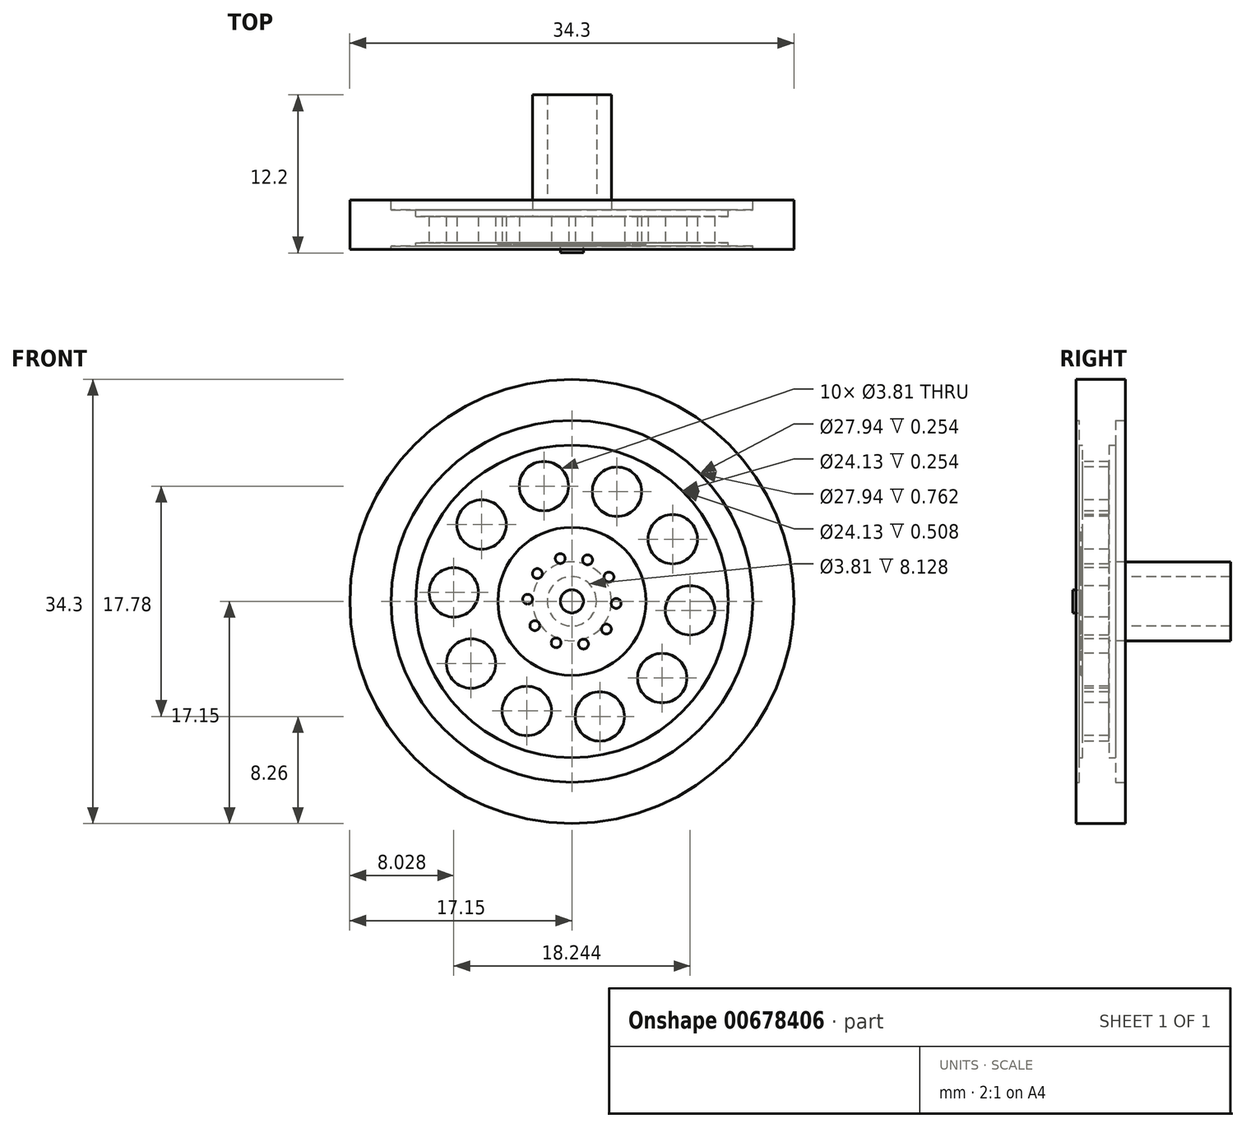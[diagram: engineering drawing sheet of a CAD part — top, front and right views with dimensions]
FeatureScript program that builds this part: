
annotation { "Feature Type Name" : "Feature", "Feature Type Description" : "" }
export const myFeature = defineFeature(function(context is Context, id is Id, definition is map)
    precondition{}
    {
        {
            var Q0;
            Q0=qCreatedBy(makeId("Front.planeOp"),FACE);
            var sketch = newSketch(context, id + "F0", { "sketchPlane" : qUnion([Q0])});
            skCircle(sketch, "E0", {"center": v(0, 0) * mm, "radius": 17.15 * mm});
            skCircle(sketch, "E1", {"center": v(0, 0) * mm, "radius": 13.97 * mm});
            skCircle(sketch, "E2", {"center": v(0, 0) * mm, "radius": 12.07 * mm});
            skCircle(sketch, "E3", {"center": v(0, 0) * mm, "radius": 5.72 * mm});
            skCircle(sketch, "E4", {"center": v(0, 0) * mm, "radius": 0.89 * mm});
            skLineSegment(sketch, "E5", {"start": v(0, 0.89) * mm, "end": v(0, 5.72) * mm});
            skPoint(sketch, "E6.center", {"position": v(0, 0.95) * mm});
            skLineSegment(sketch, "E6.anchor1", {"start": v(0, 0.95) * mm, "end": v(0, 3.3) * mm, "construction": true});
            skLineSegment(sketch, "E7", {"start": v(0, 3.3) * mm, "end": v(-0.9, 3.3) * mm});
            skLineSegment(sketch, "E8", {"start": v(0, 3.3) * mm, "end": v(0.9, 3.3) * mm});
            skCircle(sketch, "E9", {"center": v(-0.9, 3.3) * mm, "radius": 0.38 * mm});
            skCircle(sketch, "E10.1.0", {"center": v(-2.67, 2.14) * mm, "radius": 0.38 * mm});
            skCircle(sketch, "E10.2.0", {"center": v(-3.42, 0.17) * mm, "radius": 0.38 * mm});
            skCircle(sketch, "E10.3.0", {"center": v(-2.86, -1.88) * mm, "radius": 0.38 * mm});
            skCircle(sketch, "E10.4.0", {"center": v(-1.21, -3.2) * mm, "radius": 0.38 * mm});
            skCircle(sketch, "E10.5.0", {"center": v(0.9, -3.3) * mm, "radius": 0.38 * mm});
            skCircle(sketch, "E10.6.0", {"center": v(2.67, -2.14) * mm, "radius": 0.38 * mm});
            skCircle(sketch, "E10.7.0", {"center": v(3.42, -0.17) * mm, "radius": 0.38 * mm});
            skCircle(sketch, "E10.8.0", {"center": v(2.86, 1.88) * mm, "radius": 0.38 * mm});
            skCircle(sketch, "E10.9.0", {"center": v(1.21, 3.2) * mm, "radius": 0.38 * mm});
            skSolve(sketch);
        }
        {
            var Q0;
            Q0=makeQuery(id+"F0.imprint","IMPRINT",FACE,{"disambiguationData":[TD([[makeQuery(id+"F0.imprint","IMPRINT",EDGE,{"derivedFrom":sQuery(id+"F0.wireOp",EDGE,"E0")}),1.0]])]});
            extrude(context, id + "F1", {"entities" : qUnion([Q0]), "depth" : 0.76 * mm, "offsetDistance" : 25.4 * mm});
        }
        {
            var Q0;
            Q0=makeQuery(id+"F0.imprint","IMPRINT",FACE,{"disambiguationData":[TD([[makeQuery(id+"F0.imprint","IMPRINT",EDGE,{"derivedFrom":sQuery(id+"F0.wireOp",EDGE,"E1")}),1.0]])]});
            extrude(context, id + "F2", {"entities" : qUnion([Q0]), "operationType" : NewBodyOperationType.ADD, "depth" : 0.5 * mm, "offsetDistance" : 25.4 * mm});
        }
        {
            var Q0;
            Q0=makeQuery(id+"F0.imprint","IMPRINT",FACE,{"disambiguationData":[TD([[makeQuery(id+"F0.imprint","IMPRINT",EDGE,{"derivedFrom":sQuery(id+"F0.wireOp",EDGE,"E2")}),1.0]])]});
            extrude(context, id + "F3", {"entities" : qUnion([Q0]), "operationType" : NewBodyOperationType.ADD, "depth" : 0.25 * mm, "offsetDistance" : 25.4 * mm});
        }
        {
            var Q0;
            Q0=sQuery(id+"F0.wireOp",EDGE,"E3");
            extrude(context, id + "F4", {"bodyType" : ToolBodyType.SURFACE, "surfaceEntities" : qUnion([Q0]), "depth" : 0.38 * mm, "offsetDistance" : 25.4 * mm});
        }
        {
            var Q0;
            Q0=makeQuery(id+"F0.imprint","IMPRINT",FACE,{"disambiguationData":[TD([[makeQuery(id+"F0.imprint","IMPRINT",EDGE,{"derivedFrom":sQuery(id+"F0.wireOp",EDGE,"E3")}),1.0]])]});
            extrude(context, id + "F5", {"entities" : qUnion([Q0]), "operationType" : NewBodyOperationType.ADD, "depth" : 0.38 * mm, "offsetDistance" : 25.4 * mm});
        }
        {
            var Q0;
            Q0=makeQuery(id+"F0.imprint","IMPRINT",FACE,{"disambiguationData":[TD([[makeQuery(id+"F0.imprint","IMPRINT",EDGE,{"derivedFrom":sQuery(id+"F0.wireOp",EDGE,"E9")}),1.0]])]});
            var Q1;
            Q1=makeQuery(id+"F0.imprint","IMPRINT",FACE,{"disambiguationData":[TD([[makeQuery(id+"F0.imprint","IMPRINT",EDGE,{"derivedFrom":sQuery(id+"F0.wireOp",EDGE,"E10.9.0")}),1.0]])]});
            var Q2;
            Q2=makeQuery(id+"F0.imprint","IMPRINT",FACE,{"disambiguationData":[TD([[makeQuery(id+"F0.imprint","IMPRINT",EDGE,{"derivedFrom":sQuery(id+"F0.wireOp",EDGE,"E10.1.0")}),1.0]])]});
            var Q3;
            Q3=makeQuery(id+"F0.imprint","IMPRINT",FACE,{"disambiguationData":[TD([[makeQuery(id+"F0.imprint","IMPRINT",EDGE,{"derivedFrom":sQuery(id+"F0.wireOp",EDGE,"E10.8.0")}),1.0]])]});
            var Q4;
            Q4=makeQuery(id+"F0.imprint","IMPRINT",FACE,{"disambiguationData":[TD([[makeQuery(id+"F0.imprint","IMPRINT",EDGE,{"derivedFrom":sQuery(id+"F0.wireOp",EDGE,"E10.7.0")}),1.0]])]});
            var Q5;
            Q5=makeQuery(id+"F0.imprint","IMPRINT",FACE,{"disambiguationData":[TD([[makeQuery(id+"F0.imprint","IMPRINT",EDGE,{"derivedFrom":sQuery(id+"F0.wireOp",EDGE,"E10.4.0")}),1.0]])]});
            var Q6;
            Q6=makeQuery(id+"F0.imprint","IMPRINT",FACE,{"disambiguationData":[TD([[makeQuery(id+"F0.imprint","IMPRINT",EDGE,{"derivedFrom":sQuery(id+"F0.wireOp",EDGE,"E10.3.0")}),1.0]])]});
            var Q7;
            Q7=makeQuery(id+"F0.imprint","IMPRINT",FACE,{"disambiguationData":[TD([[makeQuery(id+"F0.imprint","IMPRINT",EDGE,{"derivedFrom":sQuery(id+"F0.wireOp",EDGE,"E10.2.0")}),1.0]])]});
            var Q8;
            Q8=makeQuery(id+"F0.imprint","IMPRINT",FACE,{"disambiguationData":[TD([[makeQuery(id+"F0.imprint","IMPRINT",EDGE,{"derivedFrom":sQuery(id+"F0.wireOp",EDGE,"E10.6.0")}),1.0]])]});
            var Q9;
            Q9=makeQuery(id+"F0.imprint","IMPRINT",FACE,{"disambiguationData":[TD([[makeQuery(id+"F0.imprint","IMPRINT",EDGE,{"derivedFrom":sQuery(id+"F0.wireOp",EDGE,"E10.5.0")}),1.0]])]});
            extrude(context, id + "F6", {"entities" : qUnion([Q0, Q1, Q2, Q3, Q4, Q5, Q6, Q7, Q8, Q9]), "operationType" : NewBodyOperationType.ADD, "depth" : 0.5 * mm, "offsetDistance" : 25.4 * mm});
        }
        {
            var Q0;
            Q0=makeQuery(id+"F0.imprint","IMPRINT",FACE,{"disambiguationData":[TD([[makeQuery(id+"F0.imprint","IMPRINT",EDGE,{"derivedFrom":sQuery(id+"F0.wireOp",EDGE,"E4")}),1.0]])]});
            extrude(context, id + "F7", {"entities" : qUnion([Q0]), "operationType" : NewBodyOperationType.ADD, "depth" : 1.02 * mm, "offsetDistance" : 25.4 * mm});
        }
        {
            var Q0;
            Q0=makeQuery(id+"F3.opExtrude","CAP_FACE",FACE,{"disambiguationData":[OSD([sQuery(id+"F0.wireOp",EDGE,"E2"),sQuery(id+"F0.wireOp",EDGE,"E3")])],"isStart":false});
            var sketch = newSketch(context, id + "F8", { "sketchPlane" : qUnion([Q0])});
            skLineSegment(sketch, "E11", {"start": v(0, 5.72) * mm, "end": v(0, 12.07) * mm});
            skLineSegment(sketch, "E12", {"start": v(0, 5.72) * mm, "end": v(0, 8.9) * mm});
            skLineSegment(sketch, "E13", {"start": v(0, 8.9) * mm, "end": v(-0.25, 8.9) * mm});
            skLineSegment(sketch, "E14", {"start": v(0, 8.9) * mm, "end": v(0.25, 8.9) * mm});
            skCircle(sketch, "E15", {"center": v(-2.16, 8.9) * mm, "radius": 1.9 * mm});
            skLineSegment(sketch, "E16", {"start": v(-2.16, 8.9) * mm, "end": v(-0.25, 8.9) * mm});
            skCircle(sketch, "E17.1.0", {"center": v(-6.97, 5.92) * mm, "radius": 1.9 * mm});
            skCircle(sketch, "E17.2.0", {"center": v(-9.12, 0.7) * mm, "radius": 1.9 * mm});
            skCircle(sketch, "E17.3.0", {"center": v(-7.79, -4.8) * mm, "radius": 1.9 * mm});
            skCircle(sketch, "E17.4.0", {"center": v(-3.48, -8.46) * mm, "radius": 1.9 * mm});
            skCircle(sketch, "E17.5.0", {"center": v(2.16, -8.9) * mm, "radius": 1.9 * mm});
            skCircle(sketch, "E17.6.0", {"center": v(6.97, -5.92) * mm, "radius": 1.9 * mm});
            skCircle(sketch, "E17.7.0", {"center": v(9.12, -0.7) * mm, "radius": 1.9 * mm});
            skCircle(sketch, "E17.8.0", {"center": v(7.79, 4.8) * mm, "radius": 1.9 * mm});
            skCircle(sketch, "E17.9.0", {"center": v(3.48, 8.46) * mm, "radius": 1.9 * mm});
            skPoint(sketch, "E17.center", {"position": v(0, 0) * mm});
            skSolve(sketch);
        }
        {
            var Q0;
            Q0 = qSketchRegion(id + "F8", true);
            extrude(context, id + "F9", {"entities" : qUnion([Q0]), "operationType" : NewBodyOperationType.REMOVE, "oppositeDirection" : true, "depth" : 25.4 * mm, "offsetDistance" : 25.4 * mm});
        }
        {
            var Q0;
            {var subQ0=sQuery(id+"F0.wireOp",EDGE,"E4");var subQ1=sQuery(id+"F0.wireOp",EDGE,"E10.9.0");var subQ2=sQuery(id+"F0.wireOp",EDGE,"E10.8.0");var subQ3=sQuery(id+"F0.wireOp",EDGE,"E10.7.0");var subQ4=sQuery(id+"F0.wireOp",EDGE,"E10.6.0");var subQ5=sQuery(id+"F0.wireOp",EDGE,"E10.5.0");var subQ6=sQuery(id+"F0.wireOp",EDGE,"E10.4.0");var subQ7=sQuery(id+"F0.wireOp",EDGE,"E10.3.0");var subQ8=sQuery(id+"F0.wireOp",EDGE,"E10.2.0");var subQ9=sQuery(id+"F0.wireOp",EDGE,"E10.1.0");var subQ10=sQuery(id+"F0.wireOp",EDGE,"E9");var subQ11=sQuery(id+"F0.wireOp",EDGE,"E3");var subQ12=sQuery(id+"F0.wireOp",EDGE,"E2");var subQ13=sQuery(id+"F0.wireOp",EDGE,"E1");Q0=makeQuery(id+"F7.boolean.opBoolean","MERGE",FACE,{"derivedFrom":[makeQuery(id+"F6.boolean.opBoolean","MERGE",FACE,{"derivedFrom":[makeQuery(id+"F5.boolean.opBoolean","MERGE",FACE,{"derivedFrom":[makeQuery(id+"F3.boolean.opBoolean","MERGE",FACE,{"derivedFrom":[makeQuery(id+"F2.boolean.opBoolean","MERGE",FACE,{"derivedFrom":[makeQuery(id+"F1.opExtrude","CAP_FACE",FACE,{"disambiguationData":[OSD([sQuery(id+"F0.wireOp",EDGE,"E0"),subQ13])],"isStart":true}),makeQuery(id+"F2.opExtrude","CAP_FACE",FACE,{"disambiguationData":[OSD([subQ13,subQ12])],"isStart":true})]}),makeQuery(id+"F3.opExtrude","CAP_FACE",FACE,{"disambiguationData":[OSD([subQ12,subQ11])],"isStart":true})]}),makeQuery(id+"F5.opExtrude","CAP_FACE",FACE,{"disambiguationData":[OSD([subQ11,subQ0,subQ10,subQ9,subQ8,subQ7,subQ6,subQ5,subQ4,subQ3,subQ2,subQ1])],"isStart":true})]}),makeQuery(id+"F6.opExtrude","CAP_FACE",FACE,{"disambiguationData":[OSD([subQ10])],"isStart":true}),makeQuery(id+"F6.opExtrude","CAP_FACE",FACE,{"disambiguationData":[OSD([subQ9])],"isStart":true}),makeQuery(id+"F6.opExtrude","CAP_FACE",FACE,{"disambiguationData":[OSD([subQ8])],"isStart":true}),makeQuery(id+"F6.opExtrude","CAP_FACE",FACE,{"disambiguationData":[OSD([subQ7])],"isStart":true}),makeQuery(id+"F6.opExtrude","CAP_FACE",FACE,{"disambiguationData":[OSD([subQ6])],"isStart":true}),makeQuery(id+"F6.opExtrude","CAP_FACE",FACE,{"disambiguationData":[OSD([subQ5])],"isStart":true}),makeQuery(id+"F6.opExtrude","CAP_FACE",FACE,{"disambiguationData":[OSD([subQ4])],"isStart":true}),makeQuery(id+"F6.opExtrude","CAP_FACE",FACE,{"disambiguationData":[OSD([subQ3])],"isStart":true}),makeQuery(id+"F6.opExtrude","CAP_FACE",FACE,{"disambiguationData":[OSD([subQ2])],"isStart":true}),makeQuery(id+"F6.opExtrude","CAP_FACE",FACE,{"disambiguationData":[OSD([subQ1])],"isStart":true})]}),makeQuery(id+"F7.opExtrude","CAP_FACE",FACE,{"disambiguationData":[OSD([subQ0])],"isStart":true})]});}
            extrude(context, id + "F10", {"entities" : qUnion([Q0]), "operationType" : NewBodyOperationType.ADD, "depth" : 3.05 * mm, "offsetDistance" : 25.4 * mm});
        }
        {
            var Q0;
            Q0=makeQuery(id+"F10.opExtrude","CAP_FACE",FACE,{"disambiguationData":[OSD([sQuery(id+"F0.wireOp",EDGE,"E0"),sQuery(id+"F0.wireOp",EDGE,"E1"),sQuery(id+"F0.wireOp",EDGE,"E2"),sQuery(id+"F0.wireOp",EDGE,"E3"),sQuery(id+"F0.wireOp",EDGE,"E4"),sQuery(id+"F0.wireOp",EDGE,"E9"),sQuery(id+"F0.wireOp",EDGE,"E10.1.0"),sQuery(id+"F0.wireOp",EDGE,"E10.2.0"),sQuery(id+"F0.wireOp",EDGE,"E10.3.0"),sQuery(id+"F0.wireOp",EDGE,"E10.4.0"),sQuery(id+"F0.wireOp",EDGE,"E10.5.0"),sQuery(id+"F0.wireOp",EDGE,"E10.6.0"),sQuery(id+"F0.wireOp",EDGE,"E10.7.0"),sQuery(id+"F0.wireOp",EDGE,"E10.8.0"),sQuery(id+"F0.wireOp",EDGE,"E10.9.0")])],"isStart":false});
            var sketch = newSketch(context, id + "F11", { "sketchPlane" : qUnion([Q0])});
            skCircle(sketch, "E18", {"center": v(0, 0) * mm, "radius": 3.05 * mm});
            skCircle(sketch, "E19", {"center": v(0, 0) * mm, "radius": 1.9 * mm});
            skSolve(sketch);
        }
        {
            var Q0;
            Q0 = qSketchRegion(id + "F11", true);
            extrude(context, id + "F12", {"entities" : qUnion([Q0]), "operationType" : NewBodyOperationType.ADD, "depth" : 8.13 * mm, "offsetDistance" : 25.4 * mm});
        }
        {
            var Q0;
            {var subQ1=sQuery(id+"F0.wireOp",EDGE,"E10.9.0");var subQ2=sQuery(id+"F0.wireOp",EDGE,"E10.8.0");var subQ3=sQuery(id+"F0.wireOp",EDGE,"E10.7.0");var subQ4=sQuery(id+"F0.wireOp",EDGE,"E10.6.0");var subQ5=sQuery(id+"F0.wireOp",EDGE,"E10.5.0");var subQ6=sQuery(id+"F0.wireOp",EDGE,"E10.4.0");var subQ7=sQuery(id+"F0.wireOp",EDGE,"E10.3.0");var subQ8=sQuery(id+"F0.wireOp",EDGE,"E10.2.0");var subQ9=sQuery(id+"F0.wireOp",EDGE,"E10.1.0");var subQ10=sQuery(id+"F0.wireOp",EDGE,"E9");var subQ11=sQuery(id+"F0.wireOp",EDGE,"E4");var subQ12=sQuery(id+"F0.wireOp",EDGE,"E3");var subQ13=sQuery(id+"F0.wireOp",EDGE,"E2");var subQ14=sQuery(id+"F0.wireOp",EDGE,"E1");var subQ15=sQuery(id+"F0.wireOp",EDGE,"E0");Q0=makeQuery(id+"F12.boolean.opBoolean","SPLIT",FACE,{"disambiguationData":[TD([makeQuery(id+"F1.opExtrude","SWEPT_FACE",FACE,{"disambiguationData":[OSD([subQ15])]})])],"derivedFrom":makeQuery(id+"F10.opExtrude","CAP_FACE",FACE,{"disambiguationData":[OSD([subQ15,subQ14,subQ13,subQ12,subQ11,subQ10,subQ9,subQ8,subQ7,subQ6,subQ5,subQ4,subQ3,subQ2,subQ1])],"isStart":false})});}
            var sketch = newSketch(context, id + "F13", { "sketchPlane" : qUnion([Q0])});
            skCircle(sketch, "E20", {"center": v(0, 0) * mm, "radius": 12.07 * mm});
            skCircle(sketch, "E21", {"center": v(0, 0) * mm, "radius": 13.97 * mm});
            skSolve(sketch);
        }
        {
            var Q0;
            Q0=makeQuery(id+"F13.imprint","IMPRINT",FACE,{"disambiguationData":[TD([[makeQuery(id+"F13.imprint","IMPRINT",EDGE,{"derivedFrom":sQuery(id+"F13.wireOp",EDGE,"E20")}),-1.0]])]});
            extrude(context, id + "F14", {"entities" : qUnion([Q0]), "operationType" : NewBodyOperationType.REMOVE, "oppositeDirection" : true, "depth" : 0.76 * mm, "offsetDistance" : 25.4 * mm});
        }
        {
            var Q0;
            {var subQ12=sQuery(id+"F8.wireOp",EDGE,"E15");var subQ13=makeQuery(id+"F9.boolean.opBoolean","COPY",FACE,{"derivedFrom":makeQuery(id+"F9.opExtrude","SWEPT_FACE",FACE,{"disambiguationData":[OSD([subQ12])]})});var subQ20=sQuery(id+"F0.wireOp",EDGE,"E10.9.0");var subQ21=sQuery(id+"F0.wireOp",EDGE,"E10.8.0");var subQ22=sQuery(id+"F0.wireOp",EDGE,"E10.7.0");var subQ23=sQuery(id+"F0.wireOp",EDGE,"E10.6.0");var subQ24=sQuery(id+"F0.wireOp",EDGE,"E10.5.0");var subQ25=sQuery(id+"F0.wireOp",EDGE,"E10.4.0");var subQ26=sQuery(id+"F0.wireOp",EDGE,"E10.3.0");var subQ27=sQuery(id+"F0.wireOp",EDGE,"E10.2.0");var subQ28=sQuery(id+"F0.wireOp",EDGE,"E10.1.0");var subQ29=sQuery(id+"F0.wireOp",EDGE,"E9");var subQ30=sQuery(id+"F0.wireOp",EDGE,"E4");var subQ31=sQuery(id+"F0.wireOp",EDGE,"E3");var subQ32=sQuery(id+"F0.wireOp",EDGE,"E2");var subQ33=sQuery(id+"F0.wireOp",EDGE,"E1");var subQ34=sQuery(id+"F0.wireOp",EDGE,"E0");Q0=makeQuery(id+"F14.boolean.opBoolean","SPLIT",FACE,{"disambiguationData":[TD([subQ13])],"derivedFrom":makeQuery(id+"F12.boolean.opBoolean","SPLIT",FACE,{"disambiguationData":[TD([makeQuery(id+"F1.opExtrude","SWEPT_FACE",FACE,{"disambiguationData":[OSD([subQ34])]})])],"derivedFrom":makeQuery(id+"F10.opExtrude","CAP_FACE",FACE,{"disambiguationData":[OSD([subQ34,subQ33,subQ32,subQ31,subQ30,subQ29,subQ28,subQ27,subQ26,subQ25,subQ24,subQ23,subQ22,subQ21,subQ20])],"isStart":false})})});}
            extrude(context, id + "F15", {"entities" : qUnion([Q0]), "operationType" : NewBodyOperationType.REMOVE, "oppositeDirection" : true, "depth" : 1.27 * mm, "offsetDistance" : 25.4 * mm});
        }
    });
